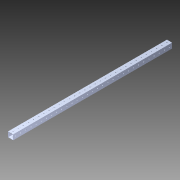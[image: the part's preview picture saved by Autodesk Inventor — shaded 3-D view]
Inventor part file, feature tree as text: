
AUTODESK INVENTOR PART (.ipt)
format: ipt  version: 2014 SP1 (Build 180222100, 222)  size: 1,282,560 bytes
history: native  units: in
note: dims shown in document units (in); Inventor stores cm internally (conversion verified against a paired STEP export)
features: pattern_circular x1, other x1, extrude x1, imported_body x1, sketch x1
ambient origin geometry x8: Origin, YZ Plane, XZ Plane, XY Plane, X Axis, Y Axis, Z Axis, Center Point
bodies: Body1 (feature_tree)
feature tree (5):
  pattern_circular  "CirPattern2"
  other  "1x1 tube1"
  extrude  "Extrusion1"  [1 undecoded]
  imported_body  "Base1"
  sketch  "Sketch1"  dims[d0=28.0in d1=0.0in]
note: 1 required parameter value undecoded (feature->parameter linkage not recoverable at this tier; creation-order binding heuristic only, values carry confidence <= 0.55)
